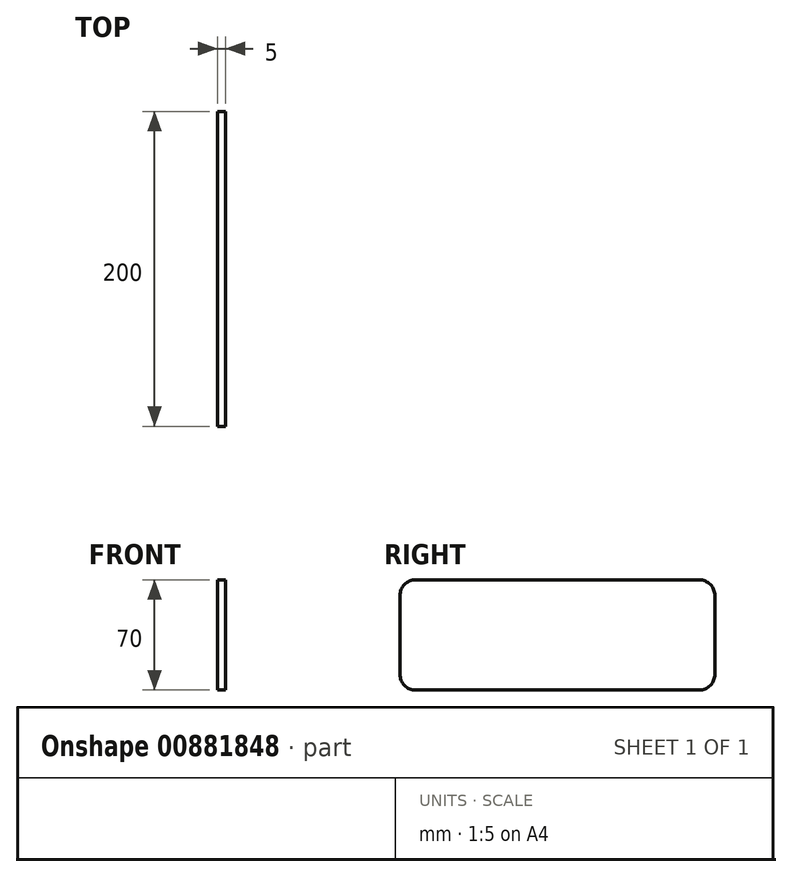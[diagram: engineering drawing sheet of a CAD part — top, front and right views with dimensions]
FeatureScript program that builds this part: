
annotation { "Feature Type Name" : "Feature", "Feature Type Description" : "" }
export const myFeature = defineFeature(function(context is Context, id is Id, definition is map)
    precondition{}
    {
        {
            var Q0;
            Q0=qCreatedBy(makeId("Right.planeOp"),FACE);
            var sketch = newSketch(context, id + "F0", { "sketchPlane" : qUnion([Q0])});
            skLineSegment(sketch, "E0.bottom", {"start": v(100, -35) * mm, "end": v(-100, -35) * mm});
            skLineSegment(sketch, "E0.top", {"start": v(100, 35) * mm, "end": v(-100, 35) * mm});
            skLineSegment(sketch, "E0.left", {"start": v(100, -35) * mm, "end": v(100, 35) * mm});
            skLineSegment(sketch, "E0.right", {"start": v(-100, -35) * mm, "end": v(-100, 35) * mm});
            skPoint(sketch, "E0.middle", {"position": v(0, 0) * mm});
            skSolve(sketch);
        }
        {
            var Q0;
            Q0=makeQuery(id+"F0.imprint","IMPRINT",FACE,{"disambiguationData":[TD([[makeQuery(id+"F0.imprint","IMPRINT",EDGE,{"derivedFrom":sQuery(id+"F0.wireOp",EDGE,"E0.bottom")}),-1.0]])]});
            extrude(context, id + "F1", {"entities" : qUnion([Q0]), "depth" : 5 * mm, "offsetDistance" : 25.4 * mm});
        }
        {
            var Q0;
            Q0=makeQuery(id+"F1.opExtrude","SWEPT_EDGE",EDGE,{"disambiguationData":[OSD([sQuery(id+"F0.wireOp",EDGE,"E0.top"),sQuery(id+"F0.wireOp",EDGE,"E0.right")])]});
            var Q1;
            Q1=makeQuery(id+"F1.opExtrude","SWEPT_EDGE",EDGE,{"disambiguationData":[OSD([sQuery(id+"F0.wireOp",EDGE,"E0.top"),sQuery(id+"F0.wireOp",EDGE,"E0.left")])]});
            var Q2;
            Q2=makeQuery(id+"F1.opExtrude","SWEPT_EDGE",EDGE,{"disambiguationData":[OSD([sQuery(id+"F0.wireOp",EDGE,"E0.bottom"),sQuery(id+"F0.wireOp",EDGE,"E0.right")])]});
            var Q3;
            Q3=makeQuery(id+"F1.opExtrude","SWEPT_EDGE",EDGE,{"disambiguationData":[OSD([sQuery(id+"F0.wireOp",EDGE,"E0.bottom"),sQuery(id+"F0.wireOp",EDGE,"E0.left")])]});
            fillet(context, id + "F2", {"entities" : qUnion([Q0, Q1, Q2, Q3]), "radius" : 10 * mm, "tangentPropagation" : true, "allowEdgeOverflow" : false});
        }
    });
